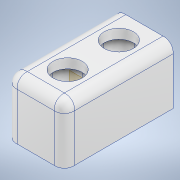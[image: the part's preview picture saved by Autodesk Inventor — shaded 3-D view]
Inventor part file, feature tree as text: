
AUTODESK INVENTOR PART (.ipt)
format: ipt  version: 2021 (Build 250183000, 183)  size: 1,488,896 bytes
history: native  units: in
note: dims shown in document units (in); Inventor stores cm internally (conversion verified against a paired STEP export)
features: extrude x10, other x9, fillet x2, sketch x2, plane x1
ambient origin geometry x8: Origin, YZ Plane, XZ Plane, XY Plane, X Axis, Y Axis, Z Axis, Center Point
bodies: Body1 (feature_tree)
feature tree (24):
  extrude  "Base"  Depth=1.7717in
  extrude  "Top"  Depth=0.1181in
  extrude  "Walls"  Depth=0.1181in
  fillet  "Outer"  Radius=1.122in
  extrude  "Wire"  Depth=0.1181in
  extrude  "Wall Holes"  Depth=0.1181in
  extrude  "Text"  Depth=0.1181in
  sketch  "Sketch16"  dims[d6=6.6929in d7=1.7717in]
  extrude  "Extrusion9"  Depth=0.1181in
  extrude  "Extrusion10"  Depth=0.1181in TaperAngle=0.0deg
  fillet  "Inner Fillet"  Radius=0.315in
  plane  "Work Plane1"
  extrude  "Wire Holes"  Depth=0.1181in
  extrude  "Extrusion13"  Depth=0.1181in
  other  "Base Sketch"
  other  "Top Sketch"
  other  "Walls Sketch"
  other  "Wire Sketch"
  other  "Wall Holes Sketch"
  other  "Text Sketch"
  other  "Support"
  sketch  "Sketch18"  dims[d8=1.7717in d9=0.0in d10=1.122in d11=1.122in d12=1.122in d13=1.122in d14=1.5748in d15=1.5748in d16=1.5748in d19=0.7087in d20=0.0in d21=0.315in d22=0.315in d23=0.2362in d24=0.2362in d25=1.4764in d26=0.0in d27=0.8976in d28=0.8976in d29=0.8976in d30=0.8976in d31=0.7874in d32=3.3465in d33=1.2992in d35=0.9843in d36=0.315in d38=0.3937in d39=0.0in d52=0.315in d55=0.1969in d56=0.0in d58=0.4528in d65=0.315in d66=0.1575in d67=0.1575in d68=0.315in d69=0.2774in d70=0.2774in d71=0.0499in d72=0.0499in d73=0.0787in d74=0.0in d77=0.6496in d81=0.9843in d82=0.0in d83=3.3465in d84=0.0in d85=0.4724in d86=0.1575in d87=0.1575in d88=0.8858in d89=0.315in d90=0.1575in d92=0.0in d93=0.1181in d94=0.0in d95=0.1575in d96=0.6496in d97=0.3937in d98=0.3937in d99=0.0in d100=0.315in d101=0.1969in d103=0.3543in d104=0.1772in d105=0.315in d106=0.0in d107=0.1575in d108=0.0in d109=0.315in d116=0.0787in d117=0.1575in d118=0.0787in d119=0.2756in d120=0.1378in d121=0.1969in d122=0.3543in d123=0.1772in d124=0.1378in d125=0.1181in d126=0.0in d44=0.0197in d45=0.0344in d46=0.0197in d47=0.0344in d48=0.0197in d49=0.0344in d59=0.0197in d60=0.0344in d61=0.0197in d62=0.0344in]
  other  "Wire Holes Sketch"
  other  "Circle E"
